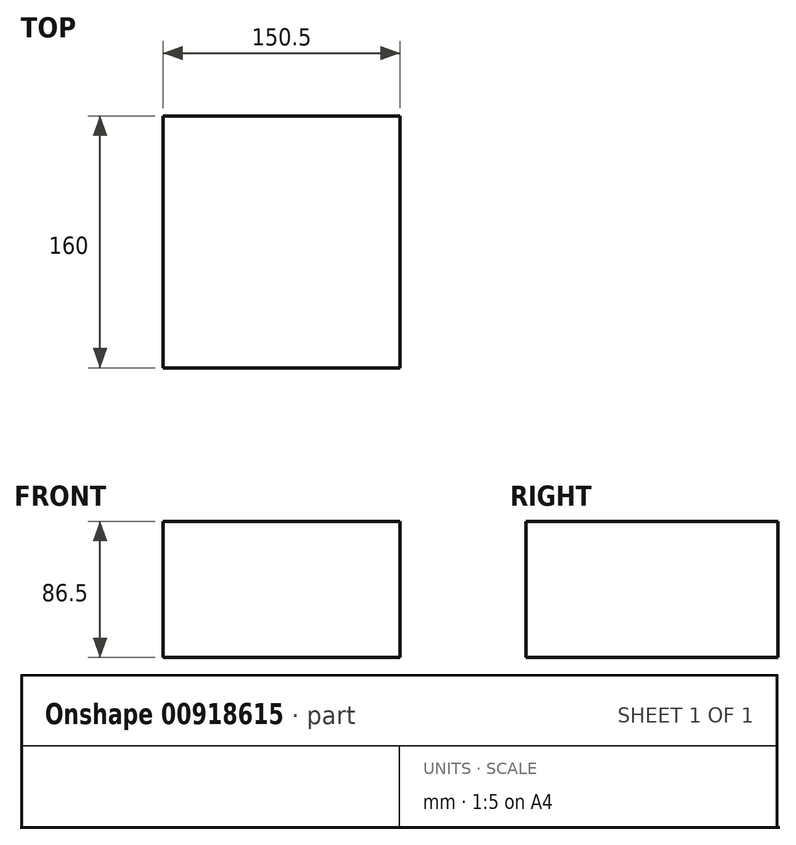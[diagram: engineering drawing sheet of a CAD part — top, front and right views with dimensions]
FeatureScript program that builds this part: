
annotation { "Feature Type Name" : "Feature", "Feature Type Description" : "" }
export const myFeature = defineFeature(function(context is Context, id is Id, definition is map)
    precondition{}
    {
        {
            var Q0;
            Q0=qCreatedBy(makeId("Front.planeOp"),FACE);
            var sketch = newSketch(context, id + "F0", { "sketchPlane" : qUnion([Q0])});
            skLineSegment(sketch, "E0.bottom", {"start": v(-75.25, 43.25) * mm, "end": v(75.25, 43.25) * mm});
            skLineSegment(sketch, "E0.top", {"start": v(-75.25, -43.25) * mm, "end": v(75.25, -43.25) * mm});
            skLineSegment(sketch, "E0.left", {"start": v(-75.25, 43.25) * mm, "end": v(-75.25, -43.25) * mm});
            skLineSegment(sketch, "E0.right", {"start": v(75.25, 43.25) * mm, "end": v(75.25, -43.25) * mm});
            skPoint(sketch, "E0.middle", {"position": v(0, 0) * mm});
            skSolve(sketch);
        }
        {
            var Q0;
            Q0=makeQuery(id+"F0.imprint","IMPRINT",FACE,{"disambiguationData":[TD([[makeQuery(id+"F0.imprint","IMPRINT",EDGE,{"derivedFrom":sQuery(id+"F0.wireOp",EDGE,"E0.bottom")}),-1.0]])]});
            extrude(context, id + "F1", {"entities" : qUnion([Q0]), "endBound" : BoundingType.SYMMETRIC, "depth" : 160 * mm, "offsetDistance" : 25 * mm});
        }
    });
